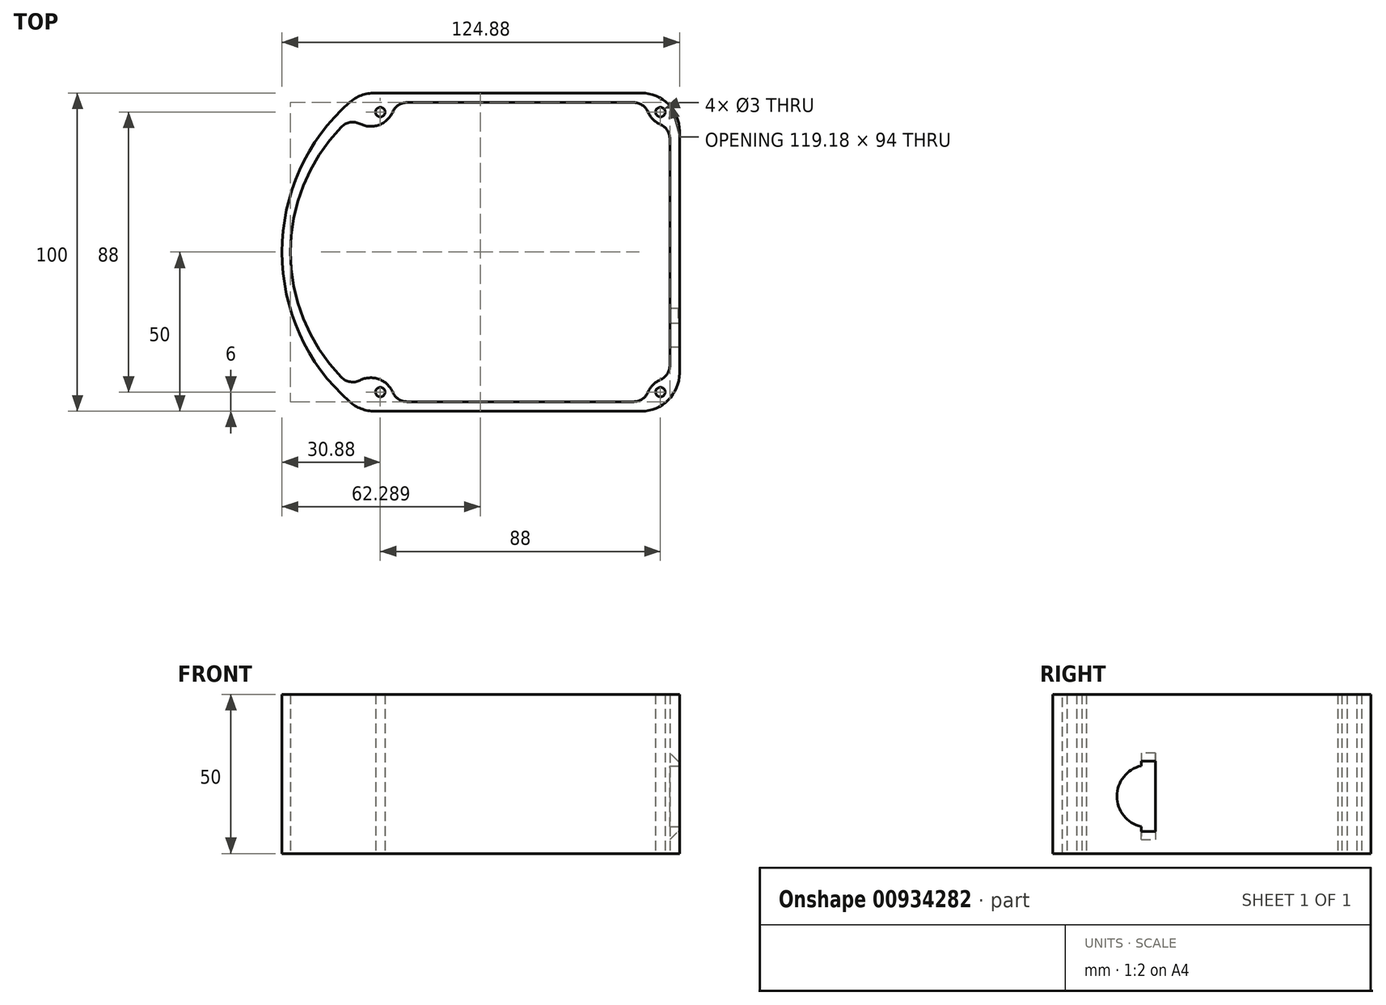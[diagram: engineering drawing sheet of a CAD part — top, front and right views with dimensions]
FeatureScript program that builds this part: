
annotation { "Feature Type Name" : "Feature", "Feature Type Description" : "" }
export const myFeature = defineFeature(function(context is Context, id is Id, definition is map)
    precondition{}
    {
        {
            var Q0;
            Q0=qCreatedBy(makeId("Top.planeOp"),FACE);
            var sketch = newSketch(context, id + "F0", { "sketchPlane" : qUnion([Q0])});
            skLineSegment(sketch, "E0.bottom", {"start": v(50, -50) * mm, "end": v(-50, -50) * mm});
            skLineSegment(sketch, "E0.top", {"start": v(50, 50) * mm, "end": v(-50, 50) * mm});
            skLineSegment(sketch, "E0.left", {"start": v(50, -50) * mm, "end": v(50, 50) * mm});
            skLineSegment(sketch, "E0.right", {"start": v(-50, -50) * mm, "end": v(-50, 50) * mm, "construction": true});
            skPoint(sketch, "E0.middle", {"position": v(0, 0) * mm});
            skLineSegment(sketch, "E1.bottom", {"start": v(47, -47) * mm, "end": v(-47, -47) * mm});
            skLineSegment(sketch, "E1.top", {"start": v(47, 47) * mm, "end": v(-47, 47) * mm});
            skLineSegment(sketch, "E1.left", {"start": v(47, -47) * mm, "end": v(47, 47) * mm});
            skLineSegment(sketch, "E1.right", {"start": v(-47, -47) * mm, "end": v(-47, 47) * mm, "construction": true});
            skLineSegment(sketch, "E2.bottom", {"start": v(-47, 47) * mm, "end": v(-44, 47) * mm, "construction": true});
            skLineSegment(sketch, "E2.top", {"start": v(-47, 44) * mm, "end": v(-44, 44) * mm, "construction": true});
            skLineSegment(sketch, "E2.left", {"start": v(-47, 47) * mm, "end": v(-47, 44) * mm, "construction": true});
            skLineSegment(sketch, "E2.right", {"start": v(-44, 47) * mm, "end": v(-44, 44) * mm, "construction": true});
            skLineSegment(sketch, "E3.bottom", {"start": v(47, 47) * mm, "end": v(44, 47) * mm, "construction": true});
            skLineSegment(sketch, "E3.top", {"start": v(47, 44) * mm, "end": v(44, 44) * mm});
            skLineSegment(sketch, "E3.left", {"start": v(47, 47) * mm, "end": v(47, 44) * mm, "construction": true});
            skLineSegment(sketch, "E3.right", {"start": v(44, 47) * mm, "end": v(44, 44) * mm});
            skLineSegment(sketch, "E4.bottom", {"start": v(47, -47) * mm, "end": v(44, -47) * mm, "construction": true});
            skLineSegment(sketch, "E4.top", {"start": v(47, -44) * mm, "end": v(44, -44) * mm, "construction": true});
            skLineSegment(sketch, "E4.left", {"start": v(47, -47) * mm, "end": v(47, -44) * mm, "construction": true});
            skLineSegment(sketch, "E4.right", {"start": v(44, -47) * mm, "end": v(44, -44) * mm, "construction": true});
            skLineSegment(sketch, "E5.bottom", {"start": v(-47, -47) * mm, "end": v(-44, -47) * mm, "construction": true});
            skLineSegment(sketch, "E5.top", {"start": v(-47, -44) * mm, "end": v(-44, -44) * mm});
            skLineSegment(sketch, "E5.left", {"start": v(-47, -47) * mm, "end": v(-47, -44) * mm, "construction": true});
            skLineSegment(sketch, "E5.right", {"start": v(-44, -47) * mm, "end": v(-44, -44) * mm});
            skCircle(sketch, "E6", {"center": v(-44, -44) * mm, "radius": 1.5 * mm});
            skCircle(sketch, "E7", {"center": v(-44, 44) * mm, "radius": 1.5 * mm});
            skCircle(sketch, "E8", {"center": v(44, 44) * mm, "radius": 1.5 * mm});
            skCircle(sketch, "E9", {"center": v(44, -44) * mm, "radius": 1.5 * mm});
            skCircle(sketch, "E10", {"center": v(-47, 47) * mm, "radius": 7.5 * mm});
            skCircle(sketch, "E11", {"center": v(47, 47) * mm, "radius": 7.5 * mm});
            skCircle(sketch, "E12", {"center": v(47, -47) * mm, "radius": 7.5 * mm});
            skCircle(sketch, "E13", {"center": v(-47, -47) * mm, "radius": 7.5 * mm});
            skArc(sketch, "E14", {"start": v(-50, 50) * mm, "mid": v(-74.88, 0) * mm, "end": v(-50, -50) * mm});
            skLineSegment(sketch, "E15", {"start": v(0, 0) * mm, "end": v(-74.86, 0) * mm});
            skArc(sketch, "E16", {"start": v(-47, 47) * mm, "mid": v(-72.18, 0) * mm, "end": v(-47, -47) * mm});
            skSolve(sketch);
        }
        {
            var Q0;
            {var subQ0=sQuery(id+"F0.wireOp",EDGE,"E13");var subQ1=sQuery(id+"F0.wireOp",EDGE,"E0.right");var subQ2=makeQuery(id+"F0.imprint","INTERSECT",VERTEX,{"derivedFrom":[subQ1,subQ0]});Q0=makeQuery(id+"F0.imprint","IMPRINT",FACE,{"disambiguationData":[TD([[makeQuery(id+"F0.imprint","IMPRINT",EDGE,{"disambiguationData":[TD([[subQ2,-1.0]])],"derivedFrom":subQ1}),-1.0]])]});}
            var Q1;
            {var subQ5=sQuery(id+"F0.wireOp",EDGE,"E0.bottom");var subQ8=sQuery(id+"F0.wireOp",EDGE,"E0.right");var subQ9=makeQuery(id+"F0.imprint","INTERSECT",VERTEX,{"derivedFrom":[subQ5,subQ8]});Q1=makeQuery(id+"F0.imprint","IMPRINT",FACE,{"disambiguationData":[TD([[makeQuery(id+"F0.imprint","IMPRINT",EDGE,{"disambiguationData":[TD([[subQ9,1.0]])],"derivedFrom":subQ5}),-1.0]])]});}
            var Q2;
            Q2=makeQuery(id+"F0.imprint","IMPRINT",FACE,{"disambiguationData":[TD([[makeQuery(id+"F0.imprint","IMPRINT",EDGE,{"derivedFrom":sQuery(id+"F0.wireOp",EDGE,"E6")}),-1.0]])]});
            var Q3;
            {var subQ0=sQuery(id+"F0.wireOp",EDGE,"E12");var subQ1=sQuery(id+"F0.wireOp",EDGE,"E0.bottom");var subQ2=makeQuery(id+"F0.imprint","INTERSECT",VERTEX,{"derivedFrom":[subQ1,subQ0]});Q3=makeQuery(id+"F0.imprint","IMPRINT",FACE,{"disambiguationData":[TD([[makeQuery(id+"F0.imprint","IMPRINT",EDGE,{"disambiguationData":[TD([[subQ2,-1.0]])],"derivedFrom":subQ1}),-1.0]])]});}
            var Q4;
            {var subQ6=sQuery(id+"F0.wireOp",EDGE,"E0.left");var subQ7=sQuery(id+"F0.wireOp",EDGE,"E0.bottom");var subQ8=makeQuery(id+"F0.imprint","INTERSECT",VERTEX,{"derivedFrom":[subQ7,subQ6]});Q4=makeQuery(id+"F0.imprint","IMPRINT",FACE,{"disambiguationData":[TD([[makeQuery(id+"F0.imprint","IMPRINT",EDGE,{"disambiguationData":[TD([[subQ8,-1.0]])],"derivedFrom":subQ7}),-1.0]])]});}
            var Q5;
            Q5=makeQuery(id+"F0.imprint","IMPRINT",FACE,{"disambiguationData":[TD([[makeQuery(id+"F0.imprint","IMPRINT",EDGE,{"derivedFrom":sQuery(id+"F0.wireOp",EDGE,"E9")}),-1.0]])]});
            var Q6;
            {var subQ0=sQuery(id+"F0.wireOp",EDGE,"E12");var subQ1=sQuery(id+"F0.wireOp",EDGE,"E0.left");var subQ2=makeQuery(id+"F0.imprint","INTERSECT",VERTEX,{"derivedFrom":[subQ1,subQ0]});Q6=makeQuery(id+"F0.imprint","IMPRINT",FACE,{"disambiguationData":[TD([[makeQuery(id+"F0.imprint","IMPRINT",EDGE,{"disambiguationData":[TD([[subQ2,-1.0]])],"derivedFrom":subQ1}),1.0]])]});}
            var Q7;
            {var subQ6=sQuery(id+"F0.wireOp",EDGE,"E0.left");var subQ7=sQuery(id+"F0.wireOp",EDGE,"E0.top");var subQ8=makeQuery(id+"F0.imprint","INTERSECT",VERTEX,{"derivedFrom":[subQ7,subQ6]});Q7=makeQuery(id+"F0.imprint","IMPRINT",FACE,{"disambiguationData":[TD([[makeQuery(id+"F0.imprint","IMPRINT",EDGE,{"disambiguationData":[TD([[subQ8,-1.0]])],"derivedFrom":subQ7}),1.0]])]});}
            var Q8;
            Q8=makeQuery(id+"F0.imprint","IMPRINT",FACE,{"disambiguationData":[TD([[makeQuery(id+"F0.imprint","IMPRINT",EDGE,{"derivedFrom":sQuery(id+"F0.wireOp",EDGE,"E8")}),-1.0]])]});
            var Q9;
            {var subQ0=sQuery(id+"F0.wireOp",EDGE,"E11");var subQ1=sQuery(id+"F0.wireOp",EDGE,"E0.top");var subQ2=makeQuery(id+"F0.imprint","INTERSECT",VERTEX,{"derivedFrom":[subQ1,subQ0]});Q9=makeQuery(id+"F0.imprint","IMPRINT",FACE,{"disambiguationData":[TD([[makeQuery(id+"F0.imprint","IMPRINT",EDGE,{"disambiguationData":[TD([[subQ2,-1.0]])],"derivedFrom":subQ1}),1.0]])]});}
            var Q10;
            {var subQ6=sQuery(id+"F0.wireOp",EDGE,"E0.top");var subQ8=sQuery(id+"F0.wireOp",EDGE,"E0.right");var subQ9=makeQuery(id+"F0.imprint","INTERSECT",VERTEX,{"derivedFrom":[subQ6,subQ8]});Q10=makeQuery(id+"F0.imprint","IMPRINT",FACE,{"disambiguationData":[TD([[makeQuery(id+"F0.imprint","IMPRINT",EDGE,{"disambiguationData":[TD([[subQ9,1.0]])],"derivedFrom":subQ6}),1.0]])]});}
            var Q11;
            Q11=makeQuery(id+"F0.imprint","IMPRINT",FACE,{"disambiguationData":[TD([[makeQuery(id+"F0.imprint","IMPRINT",EDGE,{"derivedFrom":sQuery(id+"F0.wireOp",EDGE,"E7")}),-1.0]])]});
            var Q12;
            {var subQ0=sQuery(id+"F0.wireOp",EDGE,"E16");var subQ1=makeQuery(id+"F0.imprint","IMPRINT",VERTEX,{"derivedFrom":subQ0});Q12=makeQuery(id+"F0.imprint","IMPRINT",FACE,{"disambiguationData":[TD([[makeQuery(id+"F0.imprint","IMPRINT",EDGE,{"disambiguationData":[TD([[subQ1,1.0]])],"derivedFrom":subQ0}),-1.0]])]});}
            var Q13;
            {var subQ1=sQuery(id+"F0.wireOp",EDGE,"E0.top");var subQ7=sQuery(id+"F0.wireOp",EDGE,"E14");var subQ8=makeQuery(id+"F0.imprint","INTERSECT",VERTEX,{"derivedFrom":[subQ1,subQ7]});Q13=makeQuery(id+"F0.imprint","IMPRINT",FACE,{"disambiguationData":[TD([[makeQuery(id+"F0.imprint","IMPRINT",EDGE,{"disambiguationData":[TD([[subQ8,1.0]])],"derivedFrom":subQ1}),1.0]])]});}
            var Q14;
            {var subQ8=sQuery(id+"F0.wireOp",EDGE,"E1.bottom");var subQ9=makeQuery(id+"F0.imprint","IMPRINT",VERTEX,{"derivedFrom":subQ8});Q14=makeQuery(id+"F0.imprint","IMPRINT",FACE,{"disambiguationData":[TD([[makeQuery(id+"F0.imprint","IMPRINT",EDGE,{"disambiguationData":[TD([[subQ9,1.0]])],"derivedFrom":subQ8}),1.0]])]});}
            var Q15;
            {var subQ0=sQuery(id+"F0.wireOp",EDGE,"E3.right");var subQ1=sQuery(id+"F0.wireOp",EDGE,"E1.top");var subQ2=makeQuery(id+"F0.imprint","INTERSECT",VERTEX,{"derivedFrom":[subQ1,subQ0]});Q15=makeQuery(id+"F0.imprint","IMPRINT",FACE,{"disambiguationData":[TD([[makeQuery(id+"F0.imprint","IMPRINT",EDGE,{"disambiguationData":[TD([[subQ2,-1.0]])],"derivedFrom":subQ1}),1.0]])]});}
            extrude(context, id + "F1", {"entities" : qUnion([Q0, Q1, Q2, Q3, Q4, Q5, Q6, Q7, Q8, Q9, Q10, Q11, Q12, Q13, Q14, Q15]), "depth" : 50 * mm, "offsetDistance" : 25 * mm});
        }
        {
            var Q0;
            Q0=makeQuery(id+"F1.opExtrude","SWEPT_EDGE",EDGE,{"disambiguationData":[OSD([sQuery(id+"F0.wireOp",EDGE,"E0.top"),sQuery(id+"F0.wireOp",EDGE,"E0.right")])]});
            var Q1;
            Q1=makeQuery(id+"F1.opExtrude","SWEPT_EDGE",EDGE,{"disambiguationData":[OSD([sQuery(id+"F0.wireOp",EDGE,"E0.top"),sQuery(id+"F0.wireOp",EDGE,"E0.left")])]});
            var Q2;
            Q2=makeQuery(id+"F1.opExtrude","SWEPT_EDGE",EDGE,{"disambiguationData":[OSD([sQuery(id+"F0.wireOp",EDGE,"E0.bottom"),sQuery(id+"F0.wireOp",EDGE,"E0.left")])]});
            var Q3;
            Q3=makeQuery(id+"F1.opExtrude","SWEPT_EDGE",EDGE,{"disambiguationData":[OSD([sQuery(id+"F0.wireOp",EDGE,"E0.bottom"),sQuery(id+"F0.wireOp",EDGE,"E0.right")])]});
            fillet(context, id + "F2", {"entities" : qUnion([Q0, Q1, Q2, Q3]), "radius" : 12 * mm, "tangentPropagation" : true, "allowEdgeOverflow" : false});
        }
        {
            var Q0;
            Q0=makeQuery(id+"F1.opExtrude","SWEPT_EDGE",EDGE,{"disambiguationData":[OSD([sQuery(id+"F0.wireOp",EDGE,"E1.right"),sQuery(id+"F0.wireOp",EDGE,"E13")])]});
            var Q1;
            Q1=makeQuery(id+"F1.opExtrude","SWEPT_EDGE",EDGE,{"disambiguationData":[OSD([sQuery(id+"F0.wireOp",EDGE,"E1.bottom"),sQuery(id+"F0.wireOp",EDGE,"E13")])]});
            var Q2;
            Q2=makeQuery(id+"F1.opExtrude","SWEPT_EDGE",EDGE,{"disambiguationData":[OSD([sQuery(id+"F0.wireOp",EDGE,"E1.bottom"),sQuery(id+"F0.wireOp",EDGE,"E12")])]});
            var Q3;
            Q3=makeQuery(id+"F1.opExtrude","SWEPT_EDGE",EDGE,{"disambiguationData":[OSD([sQuery(id+"F0.wireOp",EDGE,"E1.left"),sQuery(id+"F0.wireOp",EDGE,"E12")])]});
            var Q4;
            Q4=makeQuery(id+"F1.opExtrude","SWEPT_EDGE",EDGE,{"disambiguationData":[OSD([sQuery(id+"F0.wireOp",EDGE,"E1.top"),sQuery(id+"F0.wireOp",EDGE,"E11")])]});
            var Q5;
            Q5=makeQuery(id+"F1.opExtrude","SWEPT_EDGE",EDGE,{"disambiguationData":[OSD([sQuery(id+"F0.wireOp",EDGE,"E1.left"),sQuery(id+"F0.wireOp",EDGE,"E11")])]});
            var Q6;
            Q6=makeQuery(id+"F1.opExtrude","SWEPT_EDGE",EDGE,{"disambiguationData":[OSD([sQuery(id+"F0.wireOp",EDGE,"E1.right"),sQuery(id+"F0.wireOp",EDGE,"E10")])]});
            var Q7;
            Q7=makeQuery(id+"F1.opExtrude","SWEPT_EDGE",EDGE,{"disambiguationData":[OSD([sQuery(id+"F0.wireOp",EDGE,"E1.top"),sQuery(id+"F0.wireOp",EDGE,"E10")])]});
            fillet(context, id + "F3", {"entities" : qUnion([Q0, Q1, Q2, Q3, Q4, Q5, Q6, Q7]), "radius" : 5 * mm, "tangentPropagation" : true, "allowEdgeOverflow" : false});
        }
        {
            var Q0;
            Q0=makeQuery(id+"F1.opExtrude","SWEPT_FACE",FACE,{"disambiguationData":[OSD([sQuery(id+"F0.wireOp",EDGE,"E0.left")])]});
            var sketch = newSketch(context, id + "F4", { "sketchPlane" : qUnion([Q0])});
            skCircle(sketch, "E17", {"center": v(-20, 18) * mm, "radius": 9.82 * mm});
            skLineSegment(sketch, "E18.bottom", {"start": v(-17.75, 6.95) * mm, "end": v(-22.25, 6.95) * mm});
            skLineSegment(sketch, "E18.top", {"start": v(-17.75, 29.05) * mm, "end": v(-22.25, 29.05) * mm});
            skLineSegment(sketch, "E18.left", {"start": v(-17.75, 6.95) * mm, "end": v(-17.75, 29.05) * mm});
            skLineSegment(sketch, "E18.right", {"start": v(-22.25, 6.95) * mm, "end": v(-22.25, 29.05) * mm});
            skLineSegment(sketch, "E19.bottom", {"start": v(-38, 0) * mm, "end": v(-20, 0) * mm, "construction": true});
            skLineSegment(sketch, "E19.top", {"start": v(-38, 18) * mm, "end": v(-20, 18) * mm, "construction": true});
            skLineSegment(sketch, "E19.left", {"start": v(-38, 0) * mm, "end": v(-38, 18) * mm, "construction": true});
            skLineSegment(sketch, "E19.right", {"start": v(-20, 0) * mm, "end": v(-20, 18) * mm, "construction": true});
            skSolve(sketch);
        }
        {
            var Q0;
            {var subQ0=sQuery(id+"F4.wireOp",EDGE,"E18.right");var subQ1=sQuery(id+"F4.wireOp",EDGE,"E17");var subQ2=makeQuery(id+"F4.imprint","INTERSECT",VERTEX,{"disambiguationData":[OD(0.0)],"derivedFrom":[subQ1,subQ0]});Q0=makeQuery(id+"F4.imprint","IMPRINT",FACE,{"disambiguationData":[TD([[makeQuery(id+"F4.imprint","IMPRINT",EDGE,{"disambiguationData":[TD([[subQ2,-1.0]])],"derivedFrom":subQ1}),1.0]])]});}
            var Q1;
            {var subQ0=sQuery(id+"F4.wireOp",EDGE,"E18.right");var subQ1=sQuery(id+"F4.wireOp",EDGE,"E17");var subQ2=makeQuery(id+"F4.imprint","INTERSECT",VERTEX,{"disambiguationData":[OD(0.0)],"derivedFrom":[subQ1,subQ0]});Q1=makeQuery(id+"F4.imprint","IMPRINT",FACE,{"disambiguationData":[TD([[makeQuery(id+"F4.imprint","IMPRINT",EDGE,{"disambiguationData":[TD([[subQ2,1.0]])],"derivedFrom":subQ1}),1.0]])]});}
            var Q2;
            {var subQ0=sQuery(id+"F4.wireOp",EDGE,"E18.left");var subQ1=sQuery(id+"F4.wireOp",EDGE,"E17");var subQ2=makeQuery(id+"F4.imprint","INTERSECT",VERTEX,{"disambiguationData":[OD(0.0)],"derivedFrom":[subQ1,subQ0]});Q2=makeQuery(id+"F4.imprint","IMPRINT",FACE,{"disambiguationData":[TD([[makeQuery(id+"F4.imprint","IMPRINT",EDGE,{"disambiguationData":[TD([[subQ2,1.0]])],"derivedFrom":subQ1}),1.0]])]});}
            var Q3;
            {var subQ5=sQuery(id+"F4.wireOp",EDGE,"E18.top");Q3=makeQuery(id+"F4.imprint","IMPRINT",FACE,{"disambiguationData":[TD([[makeQuery(id+"F4.imprint","IMPRINT",EDGE,{"derivedFrom":subQ5}),1.0]])]});}
            var Q4;
            {var subQ5=sQuery(id+"F4.wireOp",EDGE,"E18.bottom");Q4=makeQuery(id+"F4.imprint","IMPRINT",FACE,{"disambiguationData":[TD([[makeQuery(id+"F4.imprint","IMPRINT",EDGE,{"derivedFrom":subQ5}),-1.0]])]});}
            extrude(context, id + "F5", {"entities" : qUnion([Q0, Q1, Q2, Q3, Q4]), "operationType" : NewBodyOperationType.REMOVE, "oppositeDirection" : true, "depth" : 4 * mm, "offsetDistance" : 25 * mm});
        }
        {
            var Q0;
            Q0=makeQuery(id+"F5.boolean.opBoolean","INTERSECT",EDGE,{"derivedFrom":[makeQuery(id+"F1.opExtrude","SWEPT_FACE",FACE,{"disambiguationData":[OSD([sQuery(id+"F0.wireOp",EDGE,"E1.left")])]}),makeQuery(id+"F5.opExtrude","SWEPT_FACE",FACE,{"disambiguationData":[OSD([sQuery(id+"F4.wireOp",EDGE,"E18.top")])]})]});
            var Q1;
            Q1=makeQuery(id+"F5.boolean.opBoolean","INTERSECT",EDGE,{"derivedFrom":[makeQuery(id+"F1.opExtrude","SWEPT_FACE",FACE,{"disambiguationData":[OSD([sQuery(id+"F0.wireOp",EDGE,"E1.left")])]}),makeQuery(id+"F5.opExtrude","SWEPT_FACE",FACE,{"disambiguationData":[OSD([sQuery(id+"F4.wireOp",EDGE,"E18.bottom")])]})]});
            chamfer(context, id + "F6", {"entities" : qUnion([Q0, Q1]), "width" : 2.5 * mm, "tangentPropagation" : true});
        }
    });
